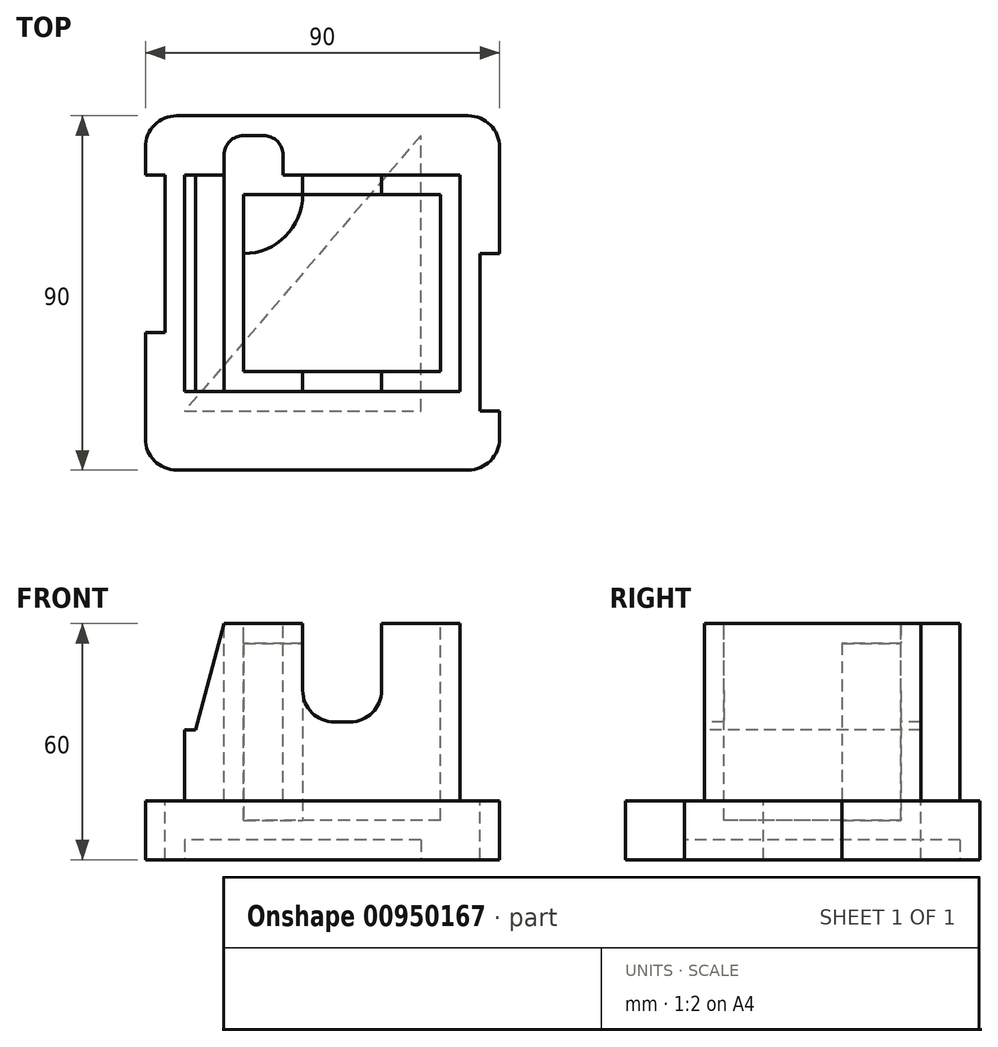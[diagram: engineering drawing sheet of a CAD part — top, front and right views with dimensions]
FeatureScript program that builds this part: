
annotation { "Feature Type Name" : "Feature", "Feature Type Description" : "" }
export const myFeature = defineFeature(function(context is Context, id is Id, definition is map)
    precondition{}
    {
        {
            var Q0;
            Q0=qCreatedBy(makeId("Front.planeOp"),FACE);
            var sketch = newSketch(context, id + "F0", { "sketchPlane" : qUnion([Q0])});
            skLineSegment(sketch, "E0", {"start": v(0, 0) * mm, "end": v(0, 18) * mm});
            skLineSegment(sketch, "E1", {"start": v(0, 18) * mm, "end": v(2.77, 18) * mm});
            skLineSegment(sketch, "E2", {"start": v(2.77, 18) * mm, "end": v(10, 45) * mm});
            skLineSegment(sketch, "E3", {"start": v(10, 45) * mm, "end": v(30, 45) * mm});
            skLineSegment(sketch, "E4", {"start": v(30, 45) * mm, "end": v(30, 20) * mm});
            skLineSegment(sketch, "E5", {"start": v(30, 20) * mm, "end": v(50, 20) * mm});
            skLineSegment(sketch, "E6", {"start": v(50, 20) * mm, "end": v(50, 45) * mm});
            skLineSegment(sketch, "E7", {"start": v(50, 45) * mm, "end": v(70, 45) * mm});
            skLineSegment(sketch, "E8", {"start": v(70, 45) * mm, "end": v(70, 0) * mm});
            skLineSegment(sketch, "E9", {"start": v(70, 0) * mm, "end": v(0, 0) * mm});
            skLineSegment(sketch, "E10", {"start": v(10, 45) * mm, "end": v(10, 0) * mm, "construction": true});
            skSolve(sketch);
        }
        {
            var Q0;
            Q0 = qSketchRegion(id + "F0", true);
            extrude(context, id + "F1", {"entities" : qUnion([Q0]), "oppositeDirection" : true, "depth" : 55 * mm, "offsetDistance" : 25 * mm});
        }
        {
            var Q0;
            Q0=makeQuery(id+"F1.opExtrude","SWEPT_EDGE",EDGE,{"disambiguationData":[OSD([sQuery(id+"F0.wireOp",EDGE,"E4"),sQuery(id+"F0.wireOp",EDGE,"E5")])]});
            var Q1;
            Q1=makeQuery(id+"F1.opExtrude","SWEPT_EDGE",EDGE,{"disambiguationData":[OSD([sQuery(id+"F0.wireOp",EDGE,"E5"),sQuery(id+"F0.wireOp",EDGE,"E6")])]});
            fillet(context, id + "F2", {"entities" : qUnion([Q0, Q1]), "radius" : 8 * mm, "tangentPropagation" : true, "allowEdgeOverflow" : false});
        }
        {
            var Q0;
            Q0=makeQuery(id+"F1.opExtrude","SWEPT_FACE",FACE,{"disambiguationData":[OSD([sQuery(id+"F0.wireOp",EDGE,"E9")])]});
            var sketch = newSketch(context, id + "F3", { "sketchPlane" : qUnion([Q0])});
            skLineSegment(sketch, "E11.bottom", {"start": v(-10, -70) * mm, "end": v(80, -70) * mm});
            skLineSegment(sketch, "E11.top", {"start": v(-10, 20) * mm, "end": v(80, 20) * mm});
            skLineSegment(sketch, "E11.left", {"start": v(-10, -70) * mm, "end": v(-10, 20) * mm});
            skLineSegment(sketch, "E11.right", {"start": v(80, -70) * mm, "end": v(80, 20) * mm});
            skSolve(sketch);
        }
        {
            var Q0;
            Q0 = qSketchRegion(id + "F3", true);
            extrude(context, id + "F4", {"entities" : qUnion([Q0]), "operationType" : NewBodyOperationType.ADD, "depth" : 15 * mm, "offsetDistance" : 25 * mm});
        }
        {
            var Q0;
            Q0=makeQuery(id+"F4.opExtrude","SWEPT_EDGE",EDGE,{"disambiguationData":[OSD([sQuery(id+"F3.wireOp",EDGE,"E11.bottom"),sQuery(id+"F3.wireOp",EDGE,"E11.left")])]});
            var Q1;
            Q1=makeQuery(id+"F4.opExtrude","SWEPT_EDGE",EDGE,{"disambiguationData":[OSD([sQuery(id+"F3.wireOp",EDGE,"E11.bottom"),sQuery(id+"F3.wireOp",EDGE,"E11.right")])]});
            var Q2;
            Q2=makeQuery(id+"F4.opExtrude","SWEPT_EDGE",EDGE,{"disambiguationData":[OSD([sQuery(id+"F3.wireOp",EDGE,"E11.top"),sQuery(id+"F3.wireOp",EDGE,"E11.left")])]});
            var Q3;
            Q3=makeQuery(id+"F4.opExtrude","SWEPT_EDGE",EDGE,{"disambiguationData":[OSD([sQuery(id+"F3.wireOp",EDGE,"E11.top"),sQuery(id+"F3.wireOp",EDGE,"E11.right")])]});
            fillet(context, id + "F5", {"entities" : qUnion([Q0, Q1, Q2, Q3]), "radius" : 8 * mm, "tangentPropagation" : true, "allowEdgeOverflow" : false});
        }
        {
            var Q0;
            Q0=makeQuery(id+"F1.opExtrude","SWEPT_FACE",FACE,{"disambiguationData":[OSD([sQuery(id+"F0.wireOp",EDGE,"E3")])]});
            var sketch = newSketch(context, id + "F6", { "sketchPlane" : qUnion([Q0])});
            skLineSegment(sketch, "E12.bottom", {"start": v(10, 55) * mm, "end": v(25, 55) * mm});
            skLineSegment(sketch, "E12.top", {"start": v(10, 65) * mm, "end": v(25, 65) * mm});
            skLineSegment(sketch, "E12.left", {"start": v(10, 55) * mm, "end": v(10, 65) * mm});
            skLineSegment(sketch, "E12.right", {"start": v(25, 55) * mm, "end": v(25, 65) * mm});
            skSolve(sketch);
        }
        {
            var Q0;
            Q0 = qSketchRegion(id + "F6", true);
            var Q1;
            Q1=makeQuery(id+"F4.opExtrude","CAP_FACE",FACE,{"disambiguationData":[OSD([sQuery(id+"F3.wireOp",EDGE,"E11.bottom"),sQuery(id+"F3.wireOp",EDGE,"E11.top"),sQuery(id+"F3.wireOp",EDGE,"E11.left"),sQuery(id+"F3.wireOp",EDGE,"E11.right")])],"isStart":true});
            extrude(context, id + "F7", {"entities" : qUnion([Q0]), "operationType" : NewBodyOperationType.ADD, "endBound" : BoundingType.UP_TO_SURFACE, "oppositeDirection" : true, "depth" : 25 * mm, "endBoundEntityFace" : qUnion([Q1]), "offsetDistance" : 25 * mm});
        }
        {
            var Q0;
            Q0=makeQuery(id+"F7.opExtrude","SWEPT_EDGE",EDGE,{"disambiguationData":[OSD([sQuery(id+"F6.wireOp",EDGE,"E12.top"),sQuery(id+"F6.wireOp",EDGE,"E12.right")])]});
            var Q1;
            Q1=makeQuery(id+"F7.opExtrude","SWEPT_EDGE",EDGE,{"disambiguationData":[OSD([sQuery(id+"F6.wireOp",EDGE,"E12.top"),sQuery(id+"F6.wireOp",EDGE,"E12.left")])]});
            fillet(context, id + "F8", {"entities" : qUnion([Q0, Q1]), "radius" : 5 * mm, "tangentPropagation" : true, "allowEdgeOverflow" : false});
        }
        {
            var Q0;
            Q0=makeQuery(id+"F7.boolean.opBoolean","MERGE",FACE,{"derivedFrom":[makeQuery(id+"F1.opExtrude","SWEPT_FACE",FACE,{"disambiguationData":[OSD([sQuery(id+"F0.wireOp",EDGE,"E3")])]}),makeQuery(id+"F7.opExtrude","CAP_FACE",FACE,{"disambiguationData":[OSD([sQuery(id+"F6.wireOp",EDGE,"E12.bottom"),sQuery(id+"F6.wireOp",EDGE,"E12.top"),sQuery(id+"F6.wireOp",EDGE,"E12.left"),sQuery(id+"F6.wireOp",EDGE,"E12.right")])],"isStart":true})]});
            var sketch = newSketch(context, id + "F9", { "sketchPlane" : qUnion([Q0])});
            skLineSegment(sketch, "E13.bottom", {"start": v(65, 50) * mm, "end": v(15, 50) * mm});
            skLineSegment(sketch, "E13.top", {"start": v(65, 5) * mm, "end": v(15, 5) * mm});
            skLineSegment(sketch, "E13.left", {"start": v(65, 50) * mm, "end": v(65, 5) * mm});
            skLineSegment(sketch, "E13.right", {"start": v(15, 50) * mm, "end": v(15, 5) * mm});
            skSolve(sketch);
        }
        {
            var Q0;
            Q0 = qSketchRegion(id + "F9", true);
            extrude(context, id + "F10", {"entities" : qUnion([Q0]), "operationType" : NewBodyOperationType.REMOVE, "oppositeDirection" : true, "depth" : 50 * mm, "offsetDistance" : 25 * mm});
        }
        {
            var Q0;
            Q0=makeQuery(id+"F10.boolean.opBoolean","COPY",FACE,{"derivedFrom":makeQuery(id+"F10.opExtrude","CAP_FACE",FACE,{"disambiguationData":[OSD([sQuery(id+"F9.wireOp",EDGE,"E13.bottom"),sQuery(id+"F9.wireOp",EDGE,"E13.top"),sQuery(id+"F9.wireOp",EDGE,"E13.left"),sQuery(id+"F9.wireOp",EDGE,"E13.right")])],"isStart":false})});
            var sketch = newSketch(context, id + "F11", { "sketchPlane" : qUnion([Q0])});
            skLineSegment(sketch, "E14", {"start": v(15, 50) * mm, "end": v(15, 35) * mm});
            skLineSegment(sketch, "E15", {"start": v(15, 50) * mm, "end": v(30, 50) * mm});
            skArc(sketch, "E16", {"start": v(15, 35) * mm, "mid": v(25.6, 39.4) * mm, "end": v(30, 50) * mm});
            skSolve(sketch);
        }
        {
            var Q0;
            Q0 = qSketchRegion(id + "F11", true);
            extrude(context, id + "F12", {"entities" : qUnion([Q0]), "operationType" : NewBodyOperationType.ADD, "depth" : 45 * mm, "offsetDistance" : 25 * mm});
        }
        {
            var Q0;
            Q0=makeQuery(id+"F4.opExtrude","CAP_FACE",FACE,{"disambiguationData":[OSD([sQuery(id+"F3.wireOp",EDGE,"E11.bottom"),sQuery(id+"F3.wireOp",EDGE,"E11.top"),sQuery(id+"F3.wireOp",EDGE,"E11.left"),sQuery(id+"F3.wireOp",EDGE,"E11.right")])],"isStart":true});
            var sketch = newSketch(context, id + "F13", { "sketchPlane" : qUnion([Q0])});
            skLineSegment(sketch, "E17.bottom", {"start": v(-10, 55) * mm, "end": v(-5, 55) * mm});
            skLineSegment(sketch, "E17.top", {"start": v(-10, 15) * mm, "end": v(-5, 15) * mm});
            skLineSegment(sketch, "E17.left", {"start": v(-10, 55) * mm, "end": v(-10, 15) * mm});
            skLineSegment(sketch, "E17.right", {"start": v(-5, 55) * mm, "end": v(-5, 15) * mm});
            skPoint(sketch, "E18.firstSnap0", {"position": v(0, 27.5) * mm});
            skPoint(sketch, "E19.firstSnap0", {"position": v(70, 35) * mm});
            skLineSegment(sketch, "E19.bottom", {"start": v(80, 35) * mm, "end": v(75, 35) * mm});
            skLineSegment(sketch, "E19.top", {"start": v(80, -5) * mm, "end": v(75, -5) * mm});
            skLineSegment(sketch, "E19.left", {"start": v(80, 35) * mm, "end": v(80, -5) * mm});
            skLineSegment(sketch, "E19.right", {"start": v(75, 35) * mm, "end": v(75, -5) * mm});
            skSolve(sketch);
        }
        {
            var Q0;
            Q0 = qSketchRegion(id + "F13", true);
            extrude(context, id + "F14", {"entities" : qUnion([Q0]), "operationType" : NewBodyOperationType.REMOVE, "endBound" : BoundingType.THROUGH_ALL, "oppositeDirection" : true, "depth" : 25 * mm, "offsetDistance" : 25 * mm});
        }
        {
            var Q0;
            Q0=makeQuery(id+"F4.opExtrude","CAP_FACE",FACE,{"disambiguationData":[OSD([sQuery(id+"F3.wireOp",EDGE,"E11.bottom"),sQuery(id+"F3.wireOp",EDGE,"E11.top"),sQuery(id+"F3.wireOp",EDGE,"E11.left"),sQuery(id+"F3.wireOp",EDGE,"E11.right")])],"isStart":false});
            var sketch = newSketch(context, id + "F15", { "sketchPlane" : qUnion([Q0])});
            skLineSegment(sketch, "E20", {"start": v(60, -65) * mm, "end": v(0, 5) * mm});
            skLineSegment(sketch, "E21", {"start": v(0, 5) * mm, "end": v(60, 5) * mm});
            skLineSegment(sketch, "E22", {"start": v(60, 5) * mm, "end": v(60, -65) * mm});
            skSolve(sketch);
        }
        {
            var Q0;
            Q0 = qSketchRegion(id + "F15", true);
            extrude(context, id + "F16", {"entities" : qUnion([Q0]), "operationType" : NewBodyOperationType.REMOVE, "oppositeDirection" : true, "depth" : 5 * mm, "offsetDistance" : 25 * mm});
        }
    });
